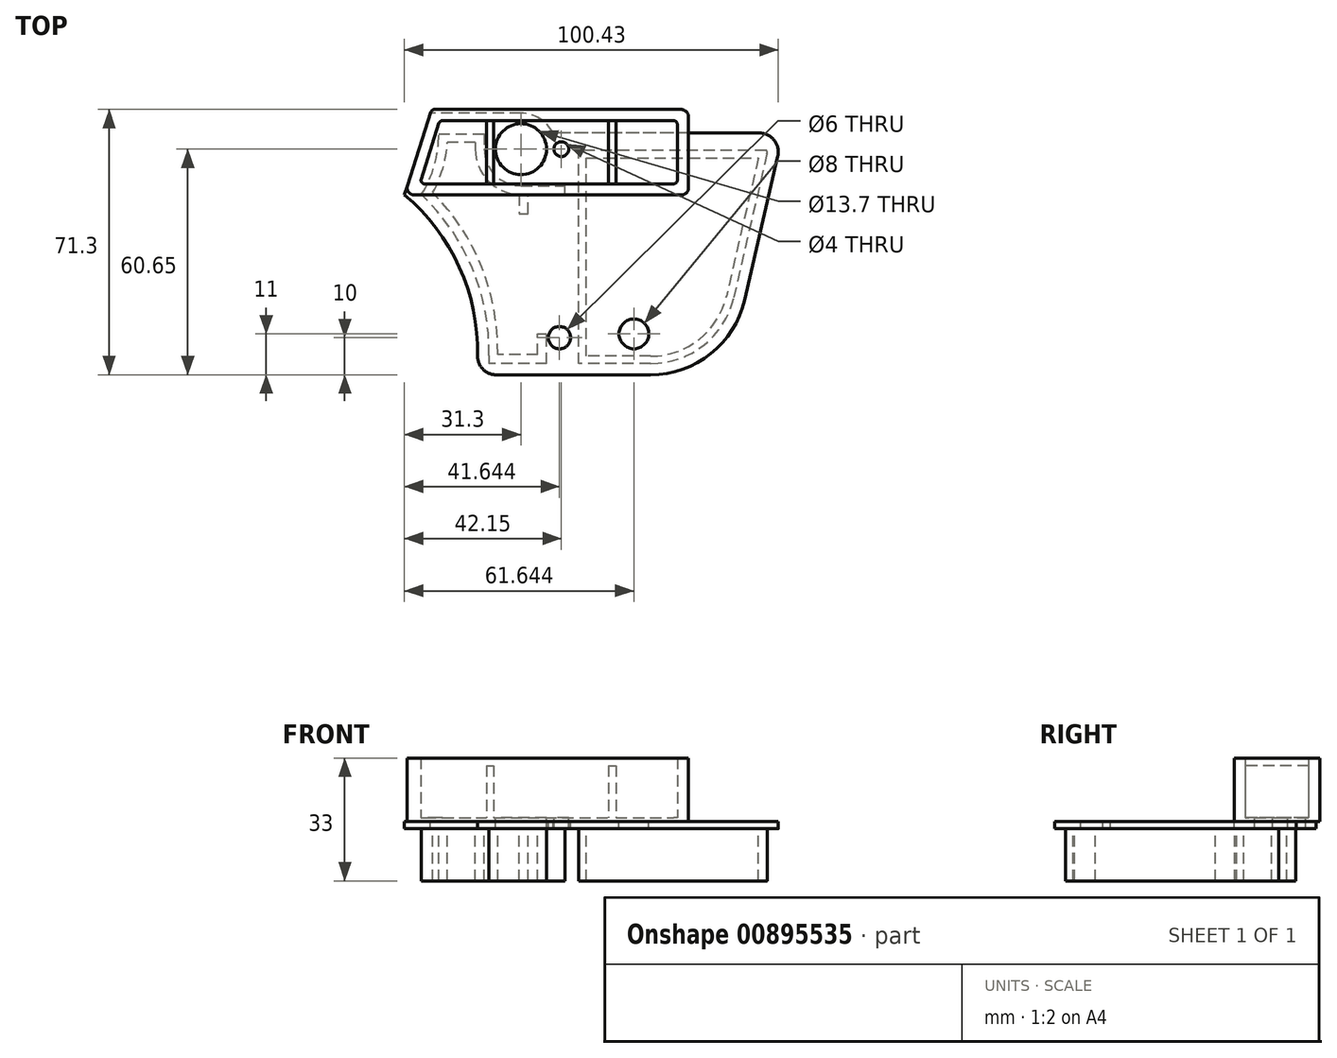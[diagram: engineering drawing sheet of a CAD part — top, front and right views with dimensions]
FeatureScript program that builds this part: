
annotation { "Feature Type Name" : "Feature", "Feature Type Description" : "" }
export const myFeature = defineFeature(function(context is Context, id is Id, definition is map)
    precondition{}
    {
        {
            var Q0;
            Q0=qCreatedBy(makeId("Top.planeOp"),FACE);
            var sketch = newSketch(context, id + "F0", { "sketchPlane" : qUnion([Q0])});
            skLineSegment(sketch, "E0.bottom", {"start": v(-68.27, 0) * mm, "end": v(-2, 0) * mm});
            skLineSegment(sketch, "E0.top", {"start": v(-73.6, -23) * mm, "end": v(-2, -23) * mm});
            skLineSegment(sketch, "E0.right", {"start": v(0, -2) * mm, "end": v(0, -21) * mm});
            skLineSegment(sketch, "E1", {"start": v(-69.22, -0.7) * mm, "end": v(-75.5, -20.4) * mm});
            skArc(sketch, "E2.filletArc", {"start": v(-75.5, -20.4) * mm, "mid": v(-75.2, -22.18) * mm, "end": v(-73.6, -23) * mm});
            skPoint(sketch, "E3.visualSharp", {"position": v(-69, 0) * mm});
            skArc(sketch, "E3.filletArc", {"start": v(-68.27, 0) * mm, "mid": v(-68.86, -0.2) * mm, "end": v(-69.22, -0.7) * mm});
            skPoint(sketch, "E4.visualSharp", {"position": v(0, 0) * mm});
            skArc(sketch, "E4.filletArc", {"start": v(0, -2) * mm, "mid": v(-0.59, -0.59) * mm, "end": v(-2, 0) * mm});
            skPoint(sketch, "E5.visualSharp", {"position": v(0, -23) * mm});
            skArc(sketch, "E5.filletArc", {"start": v(-2, -23) * mm, "mid": v(-0.59, -22.41) * mm, "end": v(0, -21) * mm});
            skLineSegment(sketch, "E6.0", {"start": v(-66.08, -3) * mm, "end": v(-4, -3) * mm});
            skLineSegment(sketch, "E6.1", {"start": v(-67.03, -3.7) * mm, "end": v(-71.81, -18.7) * mm});
            skLineSegment(sketch, "E6.2", {"start": v(-70.86, -20) * mm, "end": v(-4, -20) * mm});
            skLineSegment(sketch, "E6.3", {"start": v(-3, -4) * mm, "end": v(-3, -19) * mm});
            skPoint(sketch, "E7.visualSharp", {"position": v(-66.8, -3) * mm});
            skArc(sketch, "E7.filletArc", {"start": v(-66.08, -3) * mm, "mid": v(-66.67, -3.2) * mm, "end": v(-67.03, -3.7) * mm});
            skPoint(sketch, "E8.visualSharp", {"position": v(-3, -3) * mm});
            skArc(sketch, "E8.filletArc", {"start": v(-3, -4) * mm, "mid": v(-3.3, -3.3) * mm, "end": v(-4, -3) * mm});
            skPoint(sketch, "E9.visualSharp", {"position": v(-3, -20) * mm});
            skArc(sketch, "E9.filletArc", {"start": v(-4, -20) * mm, "mid": v(-3.3, -19.7) * mm, "end": v(-3, -19) * mm});
            skPoint(sketch, "E10.visualSharp", {"position": v(-72.23, -20) * mm});
            skArc(sketch, "E10.filletArc", {"start": v(-71.81, -18.7) * mm, "mid": v(-71.67, -19.6) * mm, "end": v(-70.86, -20) * mm});
            skLineSegment(sketch, "E11", {"start": v(-21.5, -3) * mm, "end": v(-21.5, -20) * mm});
            skLineSegment(sketch, "E12.0", {"start": v(-19.5, -3) * mm, "end": v(-19.5, -20) * mm});
            skLineSegment(sketch, "E13", {"start": v(-54.3, -3) * mm, "end": v(-54.3, -20) * mm});
            skLineSegment(sketch, "E14.0", {"start": v(-52.3, -3) * mm, "end": v(-52.3, -20) * mm});
            skSolve(sketch);
        }
        {
            var Q0;
            Q0=makeQuery(id+"F0.imprint","IMPRINT",FACE,{"disambiguationData":[TD([[makeQuery(id+"F0.imprint","IMPRINT",EDGE,{"derivedFrom":sQuery(id+"F0.wireOp",EDGE,"E0.bottom")}),-1.0]])]});
            extrude(context, id + "F1", {"entities" : qUnion([Q0]), "depth" : 17 * mm, "offsetDistance" : 25 * mm});
        }
        {
            var Q0;
            {var subQ0=sQuery(id+"F0.wireOp",EDGE,"E13");Q0=makeQuery(id+"F0.imprint","IMPRINT",FACE,{"disambiguationData":[TD([[makeQuery(id+"F0.imprint","IMPRINT",EDGE,{"derivedFrom":subQ0}),1.0]])]});}
            var Q1;
            {var subQ0=sQuery(id+"F0.wireOp",EDGE,"E11");Q1=makeQuery(id+"F0.imprint","IMPRINT",FACE,{"disambiguationData":[TD([[makeQuery(id+"F0.imprint","IMPRINT",EDGE,{"derivedFrom":subQ0}),1.0]])]});}
            extrude(context, id + "F2", {"entities" : qUnion([Q0, Q1]), "operationType" : NewBodyOperationType.ADD, "depth" : 15 * mm, "offsetDistance" : 25 * mm});
        }
        {
            var Q0;
            Q0=makeQuery(id+"F0.imprint","IMPRINT",FACE,{"disambiguationData":[TD([[makeQuery(id+"F0.imprint","IMPRINT",EDGE,{"derivedFrom":sQuery(id+"F0.wireOp",EDGE,"E6.1")}),1.0]])]});
            var Q1;
            {var subQ0=sQuery(id+"F0.wireOp",EDGE,"E11");Q1=makeQuery(id+"F0.imprint","IMPRINT",FACE,{"disambiguationData":[TD([[makeQuery(id+"F0.imprint","IMPRINT",EDGE,{"derivedFrom":subQ0}),-1.0]])]});}
            var Q2;
            Q2=makeQuery(id+"F0.imprint","IMPRINT",FACE,{"disambiguationData":[TD([[makeQuery(id+"F0.imprint","IMPRINT",EDGE,{"derivedFrom":sQuery(id+"F0.wireOp",EDGE,"E6.3")}),-1.0]])]});
            extrude(context, id + "F3", {"entities" : qUnion([Q0, Q1, Q2]), "operationType" : NewBodyOperationType.ADD, "depth" : 1 * mm, "offsetDistance" : 25 * mm});
        }
        {
            var Q0;
            Q0=qCreatedBy(makeId("Top.planeOp"),FACE);
            var sketch = newSketch(context, id + "F4", { "sketchPlane" : qUnion([Q0])});
            skLineSegment(sketch, "E15", {"start": v(19, -6.3) * mm, "end": v(-106.52, -6.3) * mm});
            skLineSegment(sketch, "E16", {"start": v(24, -12.59) * mm, "end": v(15.08, -51.23) * mm});
            skPoint(sketch, "E17.visualSharp", {"position": v(25.45, -6.3) * mm});
            skArc(sketch, "E17.filletArc", {"start": v(24, -12.59) * mm, "mid": v(23.02, -8.24) * mm, "end": v(19, -6.3) * mm});
            skLineSegment(sketch, "E18", {"start": v(-10.16, -71.3) * mm, "end": v(-51.66, -71.3) * mm});
            skPoint(sketch, "E19.visualSharp", {"position": v(10.44, -71.3) * mm});
            skArc(sketch, "E19.filletArc", {"start": v(-10.16, -71.3) * mm, "mid": v(5.97, -65.67) * mm, "end": v(15.08, -51.23) * mm});
            skLineSegment(sketch, "E20", {"start": v(-45, -1) * mm, "end": v(-74.57, -1) * mm});
            skCircle(sketch, "E21", {"center": v(-45, -10.65) * mm, "radius": 6.85 * mm});
            skArc(sketch, "E22", {"start": v(-36.39, -6.3) * mm, "mid": v(-39.94, -2.43) * mm, "end": v(-45, -1) * mm});
            skLineSegment(sketch, "E23", {"start": v(-69.32, -1) * mm, "end": v(-76.3, -22.91) * mm});
            skArc(sketch, "E24", {"start": v(-56.66, -66.2) * mm, "mid": v(-61.56, -42.32) * mm, "end": v(-76.3, -22.91) * mm});
            skPoint(sketch, "E25.visualSharp", {"position": v(-57, -71.3) * mm});
            skArc(sketch, "E25.filletArc", {"start": v(-56.66, -66.2) * mm, "mid": v(-55.23, -69.8) * mm, "end": v(-51.66, -71.3) * mm});
            skCircle(sketch, "E26", {"center": v(-34.15, -10.65) * mm, "radius": 2 * mm});
            skCircle(sketch, "E27", {"center": v(-34.66, -61.3) * mm, "radius": 3 * mm});
            skCircle(sketch, "E28", {"center": v(-14.66, -60.3) * mm, "radius": 4 * mm});
            skSolve(sketch);
        }
        {
            var Q0;
            Q0 = qSketchRegion(id + "F4", true);
            extrude(context, id + "F5", {"entities" : qUnion([Q0]), "operationType" : NewBodyOperationType.ADD, "oppositeDirection" : true, "depth" : 2 * mm, "offsetDistance" : 25 * mm});
        }
        {
            var Q0;
            {var subQ0=sQuery(id+"F0.wireOp",EDGE,"E12.0");var subQ1=sQuery(id+"F0.wireOp",EDGE,"E9.filletArc");var subQ2=sQuery(id+"F0.wireOp",EDGE,"E8.filletArc");var subQ3=sQuery(id+"F0.wireOp",EDGE,"E6.3");var subQ4=sQuery(id+"F0.wireOp",EDGE,"E6.2");var subQ5=sQuery(id+"F0.wireOp",EDGE,"E6.0");var subQ6=sQuery(id+"F0.wireOp",EDGE,"E14.0");var subQ7=sQuery(id+"F0.wireOp",EDGE,"E11");var subQ8=sQuery(id+"F0.wireOp",EDGE,"E13");var subQ9=sQuery(id+"F0.wireOp",EDGE,"E10.filletArc");var subQ10=sQuery(id+"F0.wireOp",EDGE,"E7.filletArc");var subQ11=sQuery(id+"F0.wireOp",EDGE,"E6.1");Q0=makeQuery(id+"F5.boolean.opBoolean","SPLIT",FACE,{"disambiguationData":[TD([makeQuery(id+"F5.opExtrude","SWEPT_FACE",FACE,{"disambiguationData":[OSD([sQuery(id+"F4.wireOp",EDGE,"E21")])]})])],"derivedFrom":makeQuery(id+"F3.boolean.opBoolean","MERGE",FACE,{"derivedFrom":[makeQuery(id+"F2.boolean.opBoolean","MERGE",FACE,{"derivedFrom":[makeQuery(id+"F1.opExtrude","CAP_FACE",FACE,{"disambiguationData":[OSD([sQuery(id+"F0.wireOp",EDGE,"E0.bottom"),sQuery(id+"F0.wireOp",EDGE,"E0.top"),sQuery(id+"F0.wireOp",EDGE,"E0.right"),sQuery(id+"F0.wireOp",EDGE,"E1"),sQuery(id+"F0.wireOp",EDGE,"E2.filletArc"),sQuery(id+"F0.wireOp",EDGE,"E3.filletArc"),sQuery(id+"F0.wireOp",EDGE,"E4.filletArc"),sQuery(id+"F0.wireOp",EDGE,"E5.filletArc"),subQ5,subQ11,subQ4,subQ3,subQ10,subQ2,subQ1,subQ9])],"isStart":true}),makeQuery(id+"F2.opExtrude","CAP_FACE",FACE,{"disambiguationData":[OSD([subQ5,subQ4,subQ8,subQ6])],"isStart":true}),makeQuery(id+"F2.opExtrude","CAP_FACE",FACE,{"disambiguationData":[OSD([subQ5,subQ4,subQ7,subQ0])],"isStart":true})]}),makeQuery(id+"F3.opExtrude","CAP_FACE",FACE,{"disambiguationData":[OSD([subQ5,subQ11,subQ4,subQ10,subQ9,subQ8])],"isStart":true}),makeQuery(id+"F3.opExtrude","CAP_FACE",FACE,{"disambiguationData":[OSD([subQ5,subQ4,subQ7,subQ6])],"isStart":true}),makeQuery(id+"F3.opExtrude","CAP_FACE",FACE,{"disambiguationData":[OSD([subQ5,subQ4,subQ3,subQ2,subQ1,subQ0])],"isStart":true})]})});}
            var Q1;
            {var subQ0=sQuery(id+"F0.wireOp",EDGE,"E12.0");var subQ1=sQuery(id+"F0.wireOp",EDGE,"E9.filletArc");var subQ2=sQuery(id+"F0.wireOp",EDGE,"E8.filletArc");var subQ3=sQuery(id+"F0.wireOp",EDGE,"E6.3");var subQ4=sQuery(id+"F0.wireOp",EDGE,"E6.2");var subQ5=sQuery(id+"F0.wireOp",EDGE,"E6.0");var subQ6=sQuery(id+"F0.wireOp",EDGE,"E14.0");var subQ7=sQuery(id+"F0.wireOp",EDGE,"E11");var subQ8=sQuery(id+"F0.wireOp",EDGE,"E13");var subQ9=sQuery(id+"F0.wireOp",EDGE,"E10.filletArc");var subQ10=sQuery(id+"F0.wireOp",EDGE,"E7.filletArc");var subQ11=sQuery(id+"F0.wireOp",EDGE,"E6.1");Q1=makeQuery(id+"F5.boolean.opBoolean","SPLIT",FACE,{"disambiguationData":[TD([makeQuery(id+"F5.opExtrude","SWEPT_FACE",FACE,{"disambiguationData":[OSD([sQuery(id+"F4.wireOp",EDGE,"E26")])]})])],"derivedFrom":makeQuery(id+"F3.boolean.opBoolean","MERGE",FACE,{"derivedFrom":[makeQuery(id+"F2.boolean.opBoolean","MERGE",FACE,{"derivedFrom":[makeQuery(id+"F1.opExtrude","CAP_FACE",FACE,{"disambiguationData":[OSD([sQuery(id+"F0.wireOp",EDGE,"E0.bottom"),sQuery(id+"F0.wireOp",EDGE,"E0.top"),sQuery(id+"F0.wireOp",EDGE,"E0.right"),sQuery(id+"F0.wireOp",EDGE,"E1"),sQuery(id+"F0.wireOp",EDGE,"E2.filletArc"),sQuery(id+"F0.wireOp",EDGE,"E3.filletArc"),sQuery(id+"F0.wireOp",EDGE,"E4.filletArc"),sQuery(id+"F0.wireOp",EDGE,"E5.filletArc"),subQ5,subQ11,subQ4,subQ3,subQ10,subQ2,subQ1,subQ9])],"isStart":true}),makeQuery(id+"F2.opExtrude","CAP_FACE",FACE,{"disambiguationData":[OSD([subQ5,subQ4,subQ8,subQ6])],"isStart":true}),makeQuery(id+"F2.opExtrude","CAP_FACE",FACE,{"disambiguationData":[OSD([subQ5,subQ4,subQ7,subQ0])],"isStart":true})]}),makeQuery(id+"F3.opExtrude","CAP_FACE",FACE,{"disambiguationData":[OSD([subQ5,subQ11,subQ4,subQ10,subQ9,subQ8])],"isStart":true}),makeQuery(id+"F3.opExtrude","CAP_FACE",FACE,{"disambiguationData":[OSD([subQ5,subQ4,subQ7,subQ6])],"isStart":true}),makeQuery(id+"F3.opExtrude","CAP_FACE",FACE,{"disambiguationData":[OSD([subQ5,subQ4,subQ3,subQ2,subQ1,subQ0])],"isStart":true})]})});}
            extrude(context, id + "F6", {"entities" : qUnion([Q0, Q1]), "operationType" : NewBodyOperationType.REMOVE, "oppositeDirection" : true, "depth" : 25 * mm, "offsetDistance" : 25 * mm});
        }
        {
            var Q0;
            Q0=qCreatedBy(makeId("Top.planeOp"),FACE);
            var sketch = newSketch(context, id + "F7", { "sketchPlane" : qUnion([Q0])});
            skLineSegment(sketch, "E29.1", {"start": v(-10.16, -68.3) * mm, "end": v(-29.5, -68.3) * mm});
            skArc(sketch, "E29.2", {"start": v(-10.16, -68.3) * mm, "mid": v(4.1, -63.32) * mm, "end": v(12.16, -50.55) * mm});
            skLineSegment(sketch, "E29.3", {"start": v(21.08, -11.91) * mm, "end": v(12.16, -50.55) * mm});
            skArc(sketch, "E29.4", {"start": v(21.08, -11.91) * mm, "mid": v(21.13, -11.58) * mm, "end": v(21.12, -11.25) * mm});
            skLineSegment(sketch, "E30", {"start": v(-29.5, -68.3) * mm, "end": v(-29.5, -11) * mm});
            skLineSegment(sketch, "E31.0", {"start": v(-27.5, -66.3) * mm, "end": v(-27.5, -13) * mm});
            skLineSegment(sketch, "E31.1", {"start": v(-10.16, -66.3) * mm, "end": v(-27.5, -66.3) * mm});
            skArc(sketch, "E31.2", {"start": v(-10.16, -66.3) * mm, "mid": v(2.85, -61.76) * mm, "end": v(10.2, -50.1) * mm});
            skLineSegment(sketch, "E31.3", {"start": v(18.77, -13) * mm, "end": v(10.2, -50.1) * mm});
            skLineSegment(sketch, "E32", {"start": v(-38.1, -68.3) * mm, "end": v(-53.6, -68.3) * mm});
            skArc(sketch, "E33.2", {"start": v(-53.6, -66.17) * mm, "mid": v(-58.1, -42.6) * mm, "end": v(-71.77, -22.85) * mm});
            skArc(sketch, "E34.0", {"start": v(-54.85, -10.65) * mm, "mid": v(-51.97, -17.62) * mm, "end": v(-45, -20.5) * mm});
            skLineSegment(sketch, "E35", {"start": v(-54.85, -6.5) * mm, "end": v(-54.85, -10.65) * mm});
            skLineSegment(sketch, "E36", {"start": v(-45, -20.5) * mm, "end": v(-33.2, -20.5) * mm});
            skLineSegment(sketch, "E37", {"start": v(-53.6, -66.17) * mm, "end": v(-53.6, -68.3) * mm});
            skLineSegment(sketch, "E38", {"start": v(-38.1, -68.3) * mm, "end": v(-38.1, -60.3) * mm});
            skLineSegment(sketch, "E39.0", {"start": v(-40.5, -65.9) * mm, "end": v(-40.5, -60.3) * mm});
            skLineSegment(sketch, "E39.1", {"start": v(-40.5, -65.9) * mm, "end": v(-51.21, -65.9) * mm});
            skLineSegment(sketch, "E39.5", {"start": v(-45, -22.9) * mm, "end": v(-33.2, -22.9) * mm});
            skArc(sketch, "E39.6", {"start": v(-57.25, -10.65) * mm, "mid": v(-53.66, -19.31) * mm, "end": v(-45, -22.9) * mm});
            skLineSegment(sketch, "E39.7", {"start": v(-57.25, -8.9) * mm, "end": v(-57.25, -10.65) * mm});
            skLineSegment(sketch, "E39.8", {"start": v(-57.25, -8.9) * mm, "end": v(-64.8, -8.9) * mm});
            skLineSegment(sketch, "E40", {"start": v(-33.2, -22.9) * mm, "end": v(-33.2, -20.5) * mm});
            skLineSegment(sketch, "E41", {"start": v(-40.5, -60.3) * mm, "end": v(-38.1, -60.3) * mm});
            skLineSegment(sketch, "E42", {"start": v(-45.5, -22.89) * mm, "end": v(-45.5, -28) * mm});
            skLineSegment(sketch, "E43", {"start": v(-45.5, -28) * mm, "end": v(-43.1, -28) * mm});
            skLineSegment(sketch, "E44", {"start": v(-43.1, -28) * mm, "end": v(-43.1, -22.9) * mm});
            skLineSegment(sketch, "E45", {"start": v(-51.21, -65.9) * mm, "end": v(-51.25, -65.89) * mm});
            skLineSegment(sketch, "E46.trimOffspring", {"start": v(-51.25, -65.9) * mm, "end": v(-51.26, -65.9) * mm});
            skArc(sketch, "E47.trimOffspring", {"start": v(-51.25, -65.89) * mm, "mid": v(-55.57, -42.36) * mm, "end": v(-68.69, -22.35) * mm});
            skArc(sketch, "E48", {"start": v(-71.77, -22.85) * mm, "mid": v(-68.26, -15.01) * mm, "end": v(-67.13, -6.5) * mm});
            skArc(sketch, "E49.0", {"start": v(-68.69, -22.35) * mm, "mid": v(-66, -15.84) * mm, "end": v(-64.8, -8.9) * mm});
            skLineSegment(sketch, "E50", {"start": v(20.85, -11) * mm, "end": v(-29.5, -11) * mm});
            skLineSegment(sketch, "E51", {"start": v(-67.13, -6.5) * mm, "end": v(-54.85, -6.5) * mm});
            skLineSegment(sketch, "E52", {"start": v(-27.5, -13) * mm, "end": v(18.77, -13) * mm});
            skPoint(sketch, "E53.visualSharp", {"position": v(21.09, -11) * mm});
            skArc(sketch, "E53.filletArc", {"start": v(21.12, -11.25) * mm, "mid": v(21.04, -11.07) * mm, "end": v(20.85, -11) * mm});
            skSolve(sketch);
        }
        {
            var Q0;
            Q0 = qSketchRegion(id + "F7", true);
            extrude(context, id + "F8", {"entities" : qUnion([Q0]), "operationType" : NewBodyOperationType.ADD, "oppositeDirection" : true, "depth" : 16 * mm, "offsetDistance" : 25 * mm});
        }
    });
